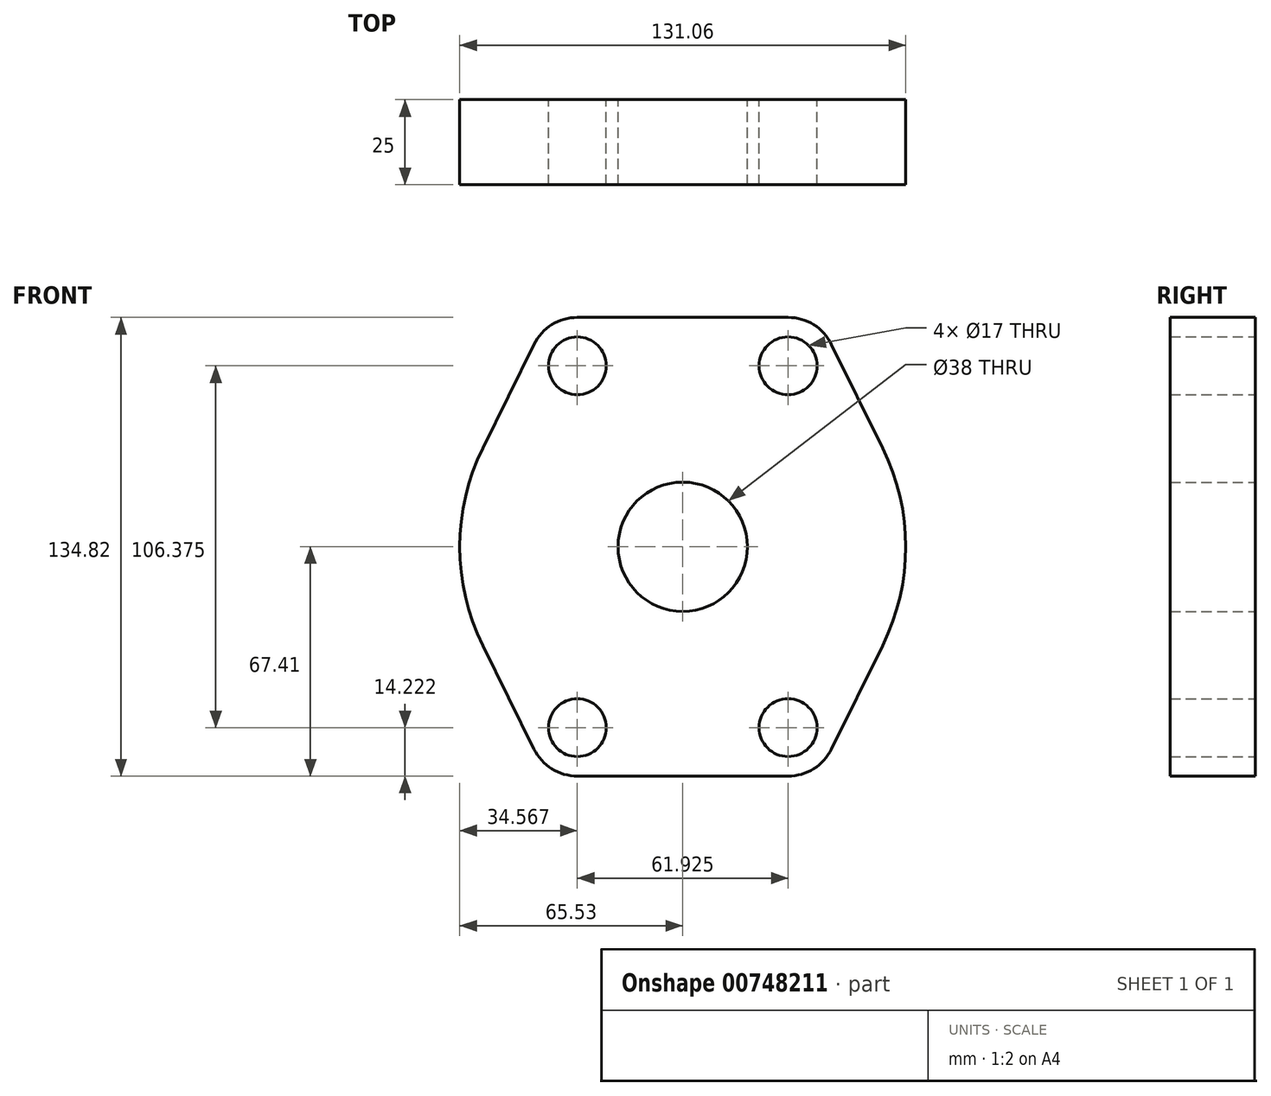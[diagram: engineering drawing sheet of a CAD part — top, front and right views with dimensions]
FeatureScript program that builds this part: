
annotation { "Feature Type Name" : "Feature", "Feature Type Description" : "" }
export const myFeature = defineFeature(function(context is Context, id is Id, definition is map)
    precondition{}
    {
        {
            var Q0;
            Q0=qCreatedBy(makeId("Front.planeOp"),FACE);
            var sketch = newSketch(context, id + "F0", { "sketchPlane" : qUnion([Q0])});
            skArc(sketch, "E0", {"start": v(-58.76, 29.01) * mm, "mid": v(-65.53, 0) * mm, "end": v(-58.76, -29.01) * mm});
            skCircle(sketch, "E1", {"center": v(-30.96, 53.19) * mm, "radius": 8.5 * mm});
            skArc(sketch, "E2.0", {"start": v(-30.96, 67.41) * mm, "mid": v(-38.47, 65.27) * mm, "end": v(-43.72, 59.48) * mm});
            skArc(sketch, "E3.0.1.0", {"start": v(-43.72, -59.48) * mm, "mid": v(-38.47, -65.27) * mm, "end": v(-30.96, -67.41) * mm});
            skCircle(sketch, "E3.0.1.1", {"center": v(-30.96, -53.19) * mm, "radius": 8.5 * mm});
            skArc(sketch, "E3.1.0.0", {"start": v(43.72, 59.48) * mm, "mid": v(38.47, 65.27) * mm, "end": v(30.96, 67.41) * mm});
            skCircle(sketch, "E3.1.0.1", {"center": v(30.96, 53.19) * mm, "radius": 8.5 * mm});
            skArc(sketch, "E3.1.1.0", {"start": v(30.96, -67.41) * mm, "mid": v(38.47, -65.27) * mm, "end": v(43.72, -59.48) * mm});
            skCircle(sketch, "E3.1.1.1", {"center": v(30.96, -53.19) * mm, "radius": 8.5 * mm});
            skLineSegment(sketch, "E3.direction1", {"start": v(-30.96, 53.19) * mm, "end": v(30.96, 53.19) * mm, "construction": true});
            skLineSegment(sketch, "E3.direction2", {"start": v(-30.96, 53.19) * mm, "end": v(-30.96, -53.19) * mm, "construction": true});
            skLineSegment(sketch, "E4", {"start": v(-30.96, -67.41) * mm, "end": v(30.96, -67.41) * mm});
            skLineSegment(sketch, "E5", {"start": v(-58.76, -29.01) * mm, "end": v(-43.72, -59.48) * mm});
            skLineSegment(sketch, "E6", {"start": v(43.72, -59.48) * mm, "end": v(58.76, -29.01) * mm});
            skLineSegment(sketch, "E7", {"start": v(43.72, 59.48) * mm, "end": v(58.76, 29.01) * mm});
            skLineSegment(sketch, "E8", {"start": v(30.96, 67.41) * mm, "end": v(-30.96, 67.41) * mm});
            skLineSegment(sketch, "E9", {"start": v(-43.72, 59.48) * mm, "end": v(-58.76, 29.01) * mm});
            skPoint(sketch, "E10.orphan", {"position": v(58.76, 29.01) * mm});
            skArc(sketch, "E11.trimOffspring", {"start": v(58.76, -29.01) * mm, "mid": v(65.53, 0) * mm, "end": v(58.76, 29.01) * mm});
            skCircle(sketch, "E12", {"center": v(0, 0) * mm, "radius": 19 * mm});
            skSolve(sketch);
        }
        {
            var Q0;
            Q0 = qSketchRegion(id + "F0", true);
            extrude(context, id + "F1", {"entities" : qUnion([Q0]), "depth" : 25 * mm, "offsetDistance" : 25 * mm});
        }
    });
